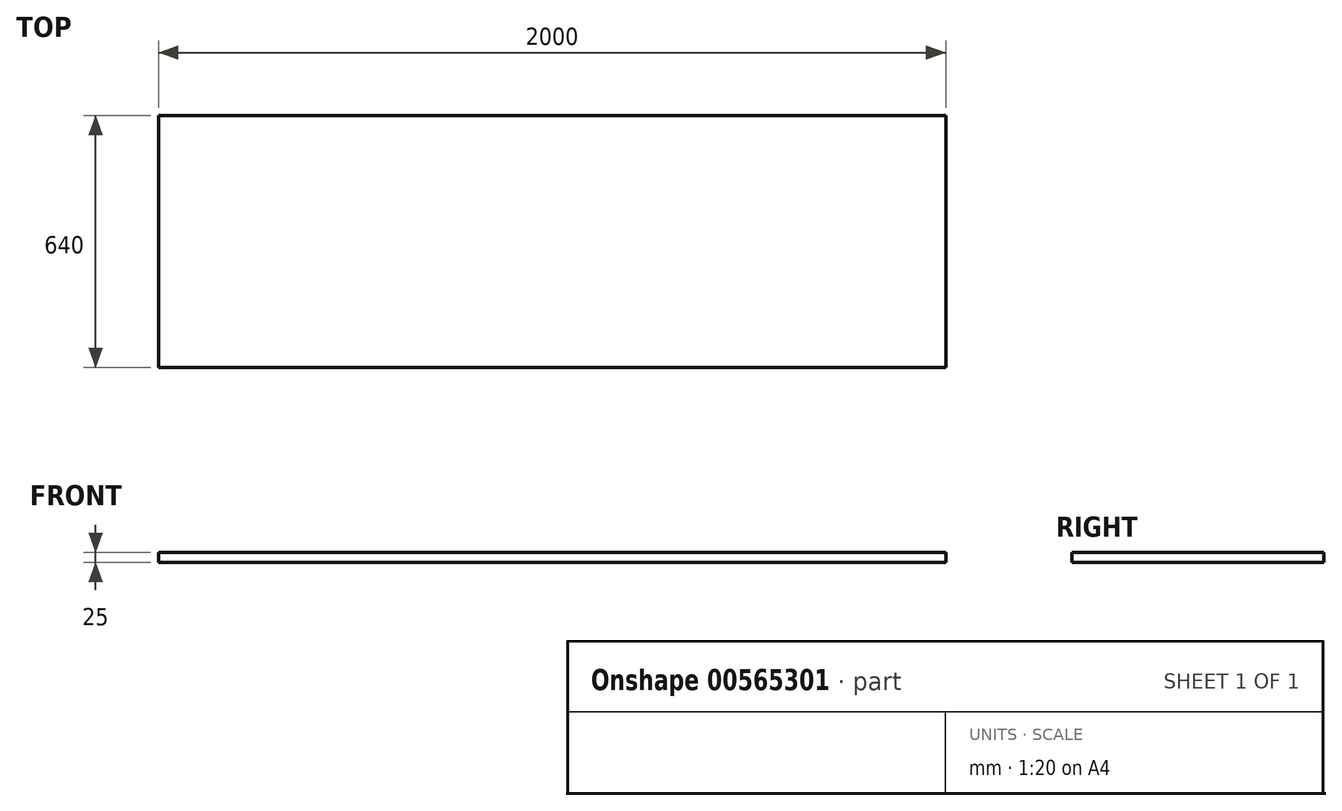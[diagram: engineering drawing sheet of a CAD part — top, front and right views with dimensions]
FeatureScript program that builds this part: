
annotation { "Feature Type Name" : "Feature", "Feature Type Description" : "" }
export const myFeature = defineFeature(function(context is Context, id is Id, definition is map)
    precondition{}
    {
        {
            var Q0;
            Q0=qCreatedBy(makeId("Front.planeOp"),FACE);
            var sketch = newSketch(context, id + "F0", { "sketchPlane" : qUnion([Q0])});
            skLineSegment(sketch, "E0.bottom", {"start": v(0, 0) * mm, "end": v(2000, 0) * mm});
            skLineSegment(sketch, "E0.top", {"start": v(0, 640) * mm, "end": v(2000, 640) * mm});
            skLineSegment(sketch, "E0.left", {"start": v(0, 0) * mm, "end": v(0, 640) * mm});
            skLineSegment(sketch, "E0.right", {"start": v(2000, 0) * mm, "end": v(2000, 640) * mm});
            skSolve(sketch);
        }
        {
            var Q0;
            Q0=qSketchRegion(id+"F0",true);
            extrude(context, id + "F1", {"entities" : qUnion([Q0]), "depth" : 25 * mm, "offsetDistance" : 25 * mm});
        }
        {
            var Q0;
            Q0=makeQuery(id+"F1.opExtrude","SWEPT_BODY",BODY,{"disambiguationData":[OSD([sQuery(id+"F0.wireOp",EDGE,"E0.bottom"),sQuery(id+"F0.wireOp",EDGE,"E0.top"),sQuery(id+"F0.wireOp",EDGE,"E0.left"),sQuery(id+"F0.wireOp",EDGE,"E0.right")])]});
            var Q1;
            Q1=makeQuery(id+"F1.opExtrude","CAP_EDGE",EDGE,{"disambiguationData":[OSD([sQuery(id+"F0.wireOp",EDGE,"E0.bottom")])],"isStart":false});
            transform(context, id + "F2", {"entities" : qUnion([Q0]), "transformType" : TransformType.ROTATION, "transformAxis" : qUnion([Q1]), "angle" : 90 * degree, "makeCopy" : false});
        }
    });
